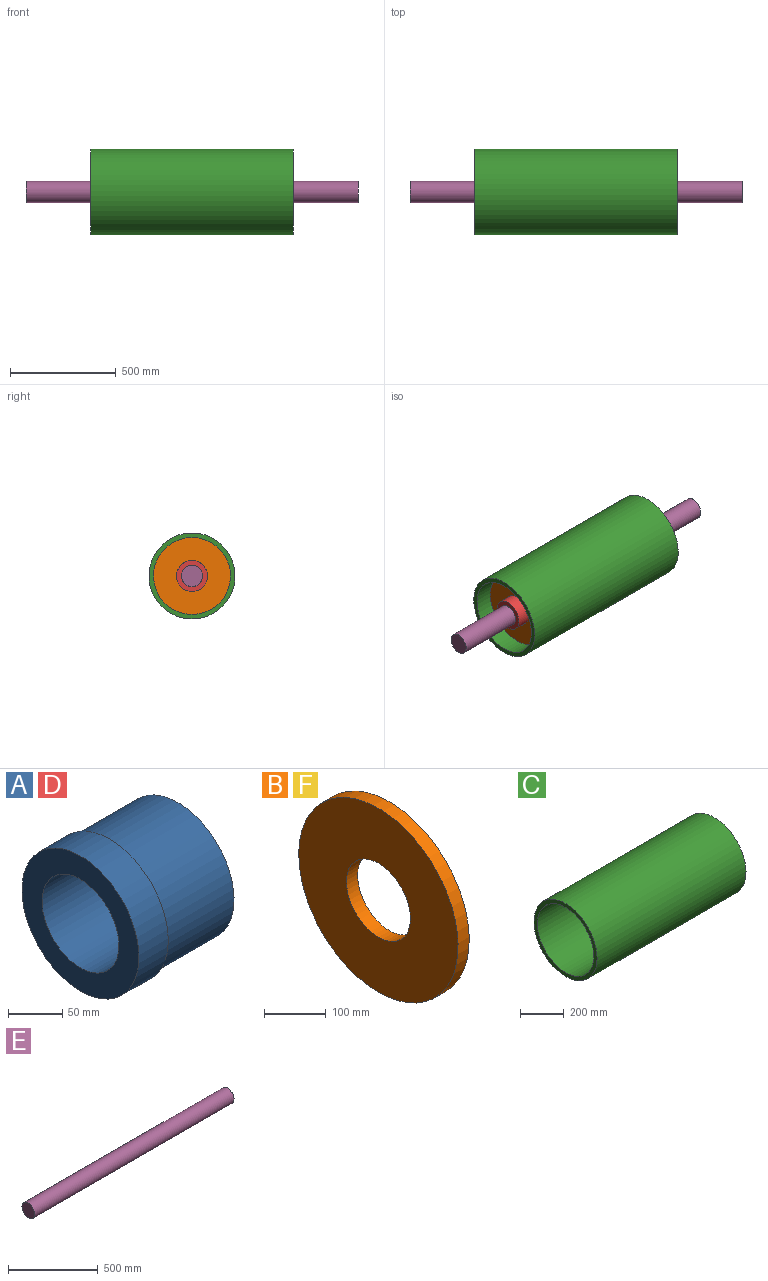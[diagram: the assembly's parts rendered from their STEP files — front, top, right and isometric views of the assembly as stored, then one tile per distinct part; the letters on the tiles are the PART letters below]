
ASSEMBLY  parts=6 mates=5
PART A: 6 faces, bbox 127x152.4x152.4 mm
  f0: cylinder r=76.2mm len=152.4mm, axis (-1,0,0), area 18241.5mm2, adj f3,f5
  f1: plane 146.05x146.05mm, normal (1,0,0), area 8897.1mm2, adj f2,f4
  f2: cylinder r=50.01mm len=127mm, axis (-1,0,0), area 39903.2mm2, adj f1,f3
  f3: plane 152.4x152.4mm, normal (-1,0,0), area 10385.5mm2, adj f0,f2
  f4: cylinder r=73.03mm len=146.05mm, axis (1,0,0), area 40790mm2, adj f1,f5
  f5: plane 152.4x152.4mm, normal (1,0,0), area 1488.5mm2, adj f0,f4
PART B: 4 faces, bbox 25.4x363.6x363.6 mm
  f0: cylinder r=73.03mm len=146.05mm, axis (-1,0,0), area 11654.3mm2, adj f2,f3
  f1: cylinder r=181.79mm len=363.58mm, axis (-1,0,0), area 29012mm2, adj f2,f3
  f2: plane 363.58x363.58mm, normal (1,0,0), area 87066.6mm2, adj f0,f1
  f3: plane 363.58x363.58mm, normal (-1,0,0), area 87066.6mm2, adj f0,f1
PART C: 4 faces, bbox 958.9x406.4x406.4 mm
  f0: cylinder r=181.79mm len=958.85mm, axis (-1,0,0), area 1095204.6mm2, adj f2,f3
  f1: cylinder r=203.2mm len=958.85mm, axis (-1,0,0), area 1224205.3mm2, adj f2,f3
  f2: plane 406.4x406.4mm, normal (1,0,0), area 25897.5mm2, adj f0,f1
  f3: plane 406.4x406.4mm, normal (-1,0,0), area 25897.5mm2, adj f0,f1
PART D: same geometry as A
PART E: 3 faces, bbox 1568.5x100x100 mm
  f0: cylinder r=50.01mm len=1568.45mm, axis (-1,0,0), area 492804.7mm2, adj f1,f2
  f1: plane 100.01x100.01mm, normal (1,0,0), area 7855.9mm2, adj f0
  f2: plane 100.01x100.01mm, normal (-1,0,0), area 7855.9mm2, adj f0
PART F: same geometry as B
PLACE A t=(390.52,0,0)mm
PLACE B t=(-377.82,0,0)mm
PLACE C at identity
PLACE D rot(axis=(0,1,0),180deg) t=(-390.52,0,0)mm
PLACE E at identity
PLACE F t=(377.83,0,0)mm
MATE fastened E.f0 <-> C.f1  axis (-1,0,0) through (0,0,0)mm
MATE revolute D.f4 <-> E.f0  axis (-1,0,0) through (-454.02,0,0)mm
MATE revolute E.f0 <-> A.f2  axis (-1,0,0) through (784.22,0,0)mm
MATE fastened F.f0 <-> A.f0  axis (-1,0,0) through (365.13,0,0)mm
MATE fastened B.f0 <-> D.f0  axis (1,0,0) through (-365.12,0,0)mm
